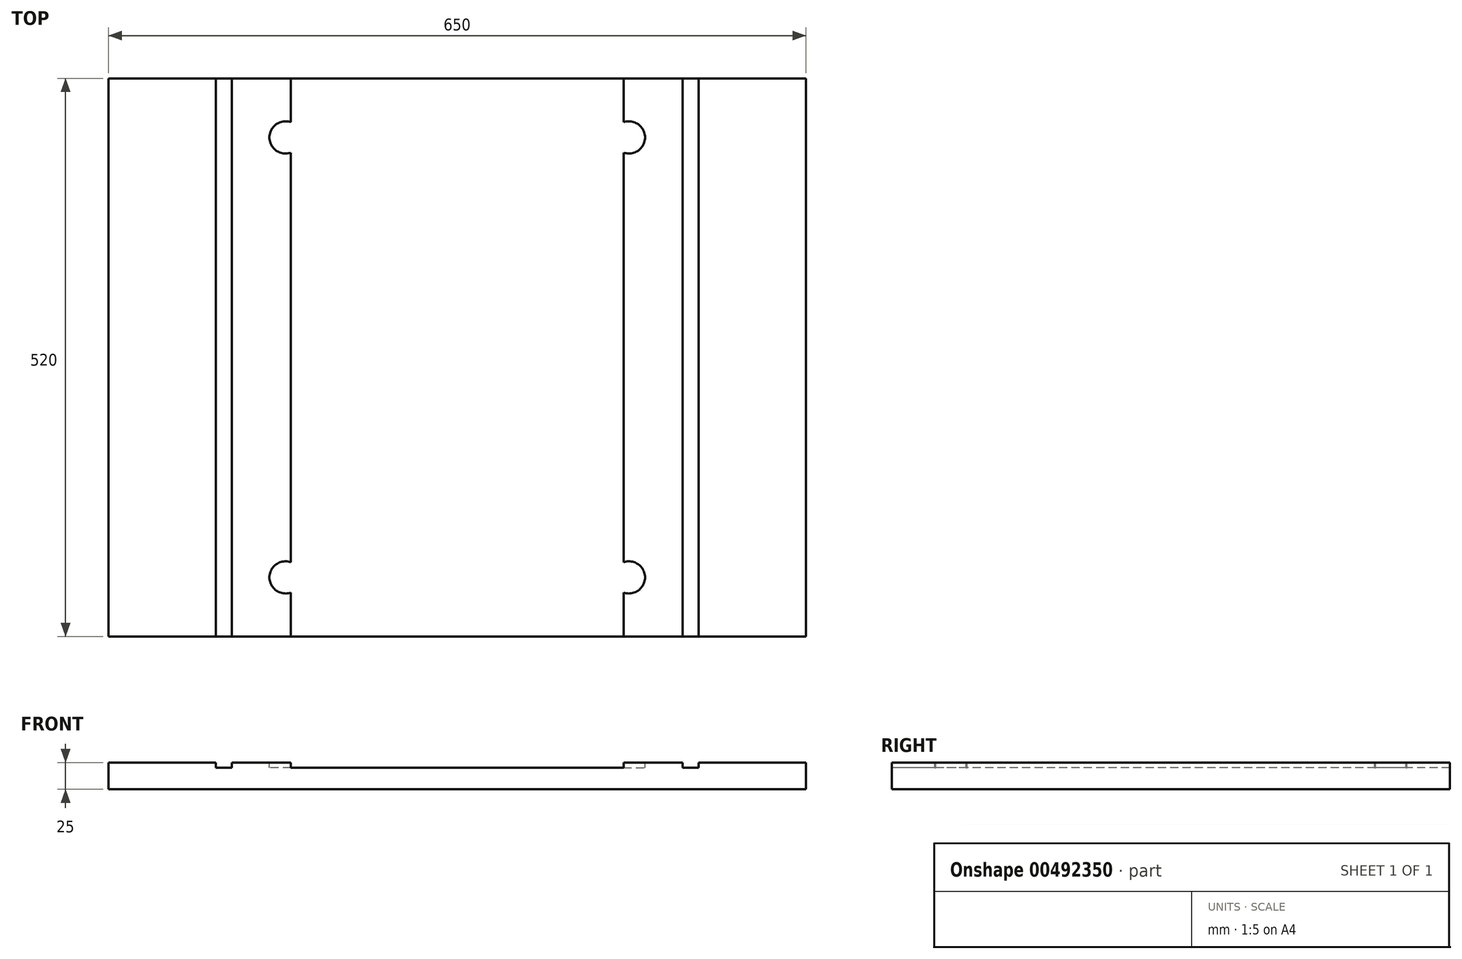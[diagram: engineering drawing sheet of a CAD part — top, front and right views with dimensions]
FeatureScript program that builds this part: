
annotation { "Feature Type Name" : "Feature", "Feature Type Description" : "" }
export const myFeature = defineFeature(function(context is Context, id is Id, definition is map)
    precondition{}
    {
        {
            var Q0;
            Q0=qCreatedBy(makeId("Top.planeOp"),FACE);
            var sketch = newSketch(context, id + "F0", { "sketchPlane" : qUnion([Q0])});
            skLineSegment(sketch, "E0.bottom", {"start": v(0, 0) * mm, "end": v(650, 0) * mm});
            skLineSegment(sketch, "E0.top", {"start": v(0, 520) * mm, "end": v(650, 520) * mm});
            skLineSegment(sketch, "E0.left", {"start": v(0, 0) * mm, "end": v(0, 520) * mm});
            skLineSegment(sketch, "E0.right", {"start": v(650, 0) * mm, "end": v(650, 520) * mm});
            skSolve(sketch);
        }
        {
            var Q0;
            Q0 = qSketchRegion(id + "F0", true);
            extrude(context, id + "F1", {"entities" : qUnion([Q0]), "depth" : 25 * mm});
        }
        {
            var Q0;
            Q0=makeQuery(id+"F1.opExtrude","CAP_FACE",FACE,{"disambiguationData":[OSD([sQuery(id+"F0.wireOp",EDGE,"E0.bottom"),sQuery(id+"F0.wireOp",EDGE,"E0.top"),sQuery(id+"F0.wireOp",EDGE,"E0.left"),sQuery(id+"F0.wireOp",EDGE,"E0.right")])],"isStart":false});
            var sketch = newSketch(context, id + "F2", { "sketchPlane" : qUnion([Q0])});
            skLineSegment(sketch, "E1.bottom", {"start": v(100, 0) * mm, "end": v(115, 0) * mm});
            skLineSegment(sketch, "E1.top", {"start": v(100, 520) * mm, "end": v(115, 520) * mm});
            skLineSegment(sketch, "E1.left", {"start": v(100, 0) * mm, "end": v(100, 520) * mm});
            skLineSegment(sketch, "E1.right", {"start": v(115, 0) * mm, "end": v(115, 520) * mm});
            skLineSegment(sketch, "E2.bottom", {"start": v(535, 520) * mm, "end": v(550, 520) * mm});
            skLineSegment(sketch, "E2.top", {"start": v(535, 0) * mm, "end": v(550, 0) * mm});
            skLineSegment(sketch, "E2.left", {"start": v(535, 520) * mm, "end": v(535, 0) * mm});
            skLineSegment(sketch, "E2.right", {"start": v(550, 520) * mm, "end": v(550, 0) * mm});
            skCircle(sketch, "E3", {"center": v(165, 465) * mm, "radius": 15 * mm});
            skLineSegment(sketch, "E4.bottom", {"start": v(165, 465) * mm, "end": v(485, 465) * mm, "construction": true});
            skLineSegment(sketch, "E4.top", {"start": v(165, 55) * mm, "end": v(485, 55) * mm, "construction": true});
            skLineSegment(sketch, "E4.left", {"start": v(165, 465) * mm, "end": v(165, 55) * mm, "construction": true});
            skLineSegment(sketch, "E4.right", {"start": v(485, 465) * mm, "end": v(485, 55) * mm, "construction": true});
            skCircle(sketch, "E5", {"center": v(485, 465) * mm, "radius": 15 * mm});
            skCircle(sketch, "E6", {"center": v(485, 55) * mm, "radius": 15 * mm});
            skCircle(sketch, "E7", {"center": v(165, 55) * mm, "radius": 15 * mm});
            skLineSegment(sketch, "E8.bottom", {"start": v(170, 520) * mm, "end": v(480, 520) * mm});
            skLineSegment(sketch, "E8.top", {"start": v(170, 0) * mm, "end": v(480, 0) * mm});
            skLineSegment(sketch, "E8.left", {"start": v(170, 520) * mm, "end": v(170, 0) * mm});
            skLineSegment(sketch, "E8.right", {"start": v(480, 520) * mm, "end": v(480, 0) * mm});
            skSolve(sketch);
        }
        {
            var Q0;
            Q0 = qSketchRegion(id + "F2", true);
            extrude(context, id + "F3", {"entities" : qUnion([Q0]), "operationType" : NewBodyOperationType.REMOVE, "oppositeDirection" : true, "offsetDistance" : 25 * mm, "depth" : 5 * mm});
        }
    });
